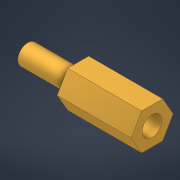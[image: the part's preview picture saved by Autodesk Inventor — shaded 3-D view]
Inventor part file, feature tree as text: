
AUTODESK INVENTOR PART (.ipt)
format: ipt  version: 2022 (Build 260153000, 153)  size: 108,544 bytes
history: native  units: in
note: dims shown in document units (in); Inventor stores cm internally (conversion verified against a paired STEP export)
features: extrude x3, sketch x3
ambient origin geometry x8: Origin, YZ Plane, XZ Plane, XY Plane, X Axis, Y Axis, Z Axis, Center Point
bodies: Solid1 (feature_tree)
feature tree (6):
  extrude  "Extrusion1"  Depth=0.4402in TaperAngle=0.0deg
  extrude  "Extrusion2"  Depth=0.3in TaperAngle=0.0deg
  extrude  "Extrusion3"  Depth=0.2362in TaperAngle=0.0deg
  sketch  "Sketch1"  dims[d1=0.2165in d2=0.4402in d3=0.0in]
  sketch  "Sketch2"  dims[d4=0.1181in d5=0.3in d6=0.0in]
  sketch  "Sketch3"  dims[d7=0.1181in d8=0.2362in d9=0.0in]
